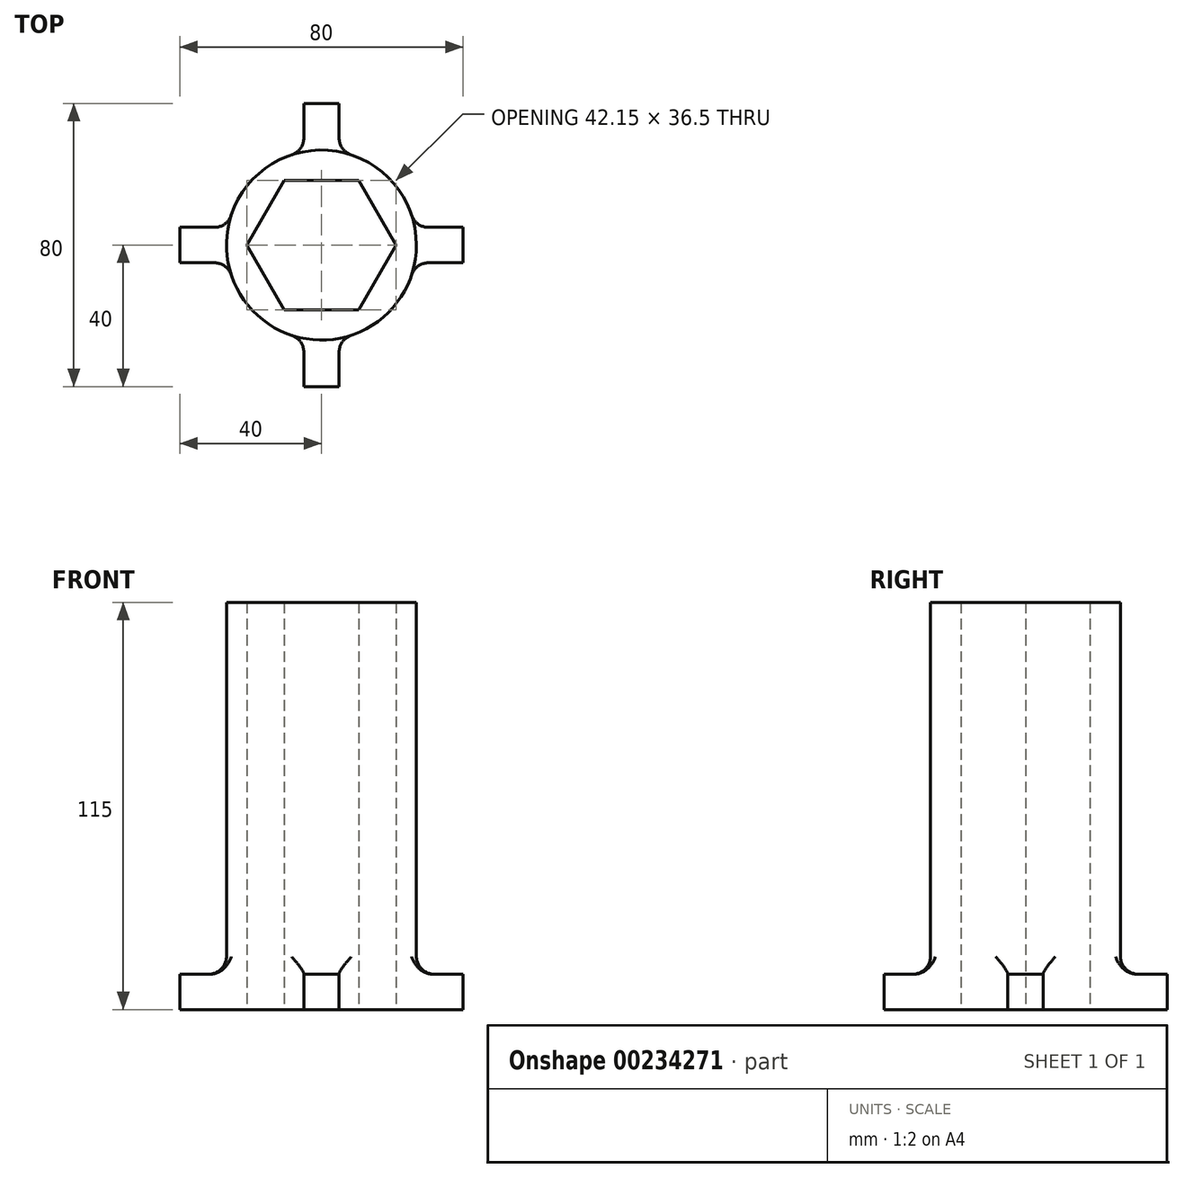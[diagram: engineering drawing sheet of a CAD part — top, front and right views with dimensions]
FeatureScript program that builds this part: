
annotation { "Feature Type Name" : "Feature", "Feature Type Description" : "" }
export const myFeature = defineFeature(function(context is Context, id is Id, definition is map)
    precondition{}
    {
        {
            var Q0;
            Q0=qCreatedBy(makeId("Top.planeOp"),FACE);
            var sketch = newSketch(context, id + "F0", { "sketchPlane" : qUnion([Q0])});
            skLineSegment(sketch, "E0", {"start": v(-10.54, 18.25) * mm, "end": v(10.54, 18.25) * mm});
            skLineSegment(sketch, "E1", {"start": v(10.54, 18.25) * mm, "end": v(21.07, 0) * mm});
            skLineSegment(sketch, "E2", {"start": v(21.07, 0) * mm, "end": v(10.54, -18.25) * mm});
            skLineSegment(sketch, "E3", {"start": v(10.54, -18.25) * mm, "end": v(-10.54, -18.25) * mm});
            skLineSegment(sketch, "E4", {"start": v(-10.54, -18.25) * mm, "end": v(-21.07, 0) * mm});
            skLineSegment(sketch, "E5", {"start": v(-21.07, 0) * mm, "end": v(-10.54, 18.25) * mm});
            skCircle(sketch, "E6", {"center": v(0, 0) * mm, "radius": 21.07 * mm, "construction": true});
            skLineSegment(sketch, "E7", {"start": v(0, 0) * mm, "end": v(-13.42, 23.25) * mm, "construction": true});
            skCircle(sketch, "E8", {"center": v(0, 0) * mm, "radius": 26.85 * mm});
            skSolve(sketch);
        }
        {
            var Q0;
            Q0=makeQuery(id+"F0.imprint","IMPRINT",FACE,{"disambiguationData":[TD([[makeQuery(id+"F0.imprint","IMPRINT",EDGE,{"derivedFrom":sQuery(id+"F0.wireOp",EDGE,"E0")}),1.0]])]});
            extrude(context, id + "F1", {"entities" : qUnion([Q0]), "depth" : 115 * mm});
        }
        {
            var Q0;
            Q0=qCreatedBy(makeId("Top.planeOp"),FACE);
            var sketch = newSketch(context, id + "F2", { "sketchPlane" : qUnion([Q0])});
            skLineSegment(sketch, "E9", {"start": v(0, 0) * mm, "end": v(-40, 0) * mm, "construction": true});
            skLineSegment(sketch, "E10", {"start": v(-40, 0) * mm, "end": v(-40, 5) * mm});
            skLineSegment(sketch, "E11", {"start": v(-40, 5) * mm, "end": v(-21.07, 5) * mm});
            skLineSegment(sketch, "E12", {"start": v(-21.07, 5) * mm, "end": v(-21.07, 0) * mm});
            skLineSegment(sketch, "E13.MirrorCS", {"start": v(-21.07, -5) * mm, "end": v(-21.07, 0) * mm});
            skLineSegment(sketch, "E14.MirrorCS", {"start": v(-40, -5) * mm, "end": v(-21.07, -5) * mm});
            skLineSegment(sketch, "E15.MirrorCS", {"start": v(-40, 0) * mm, "end": v(-40, -5) * mm});
            skLineSegment(sketch, "E16.1.0", {"start": v(-5, 40) * mm, "end": v(-5, 21.07) * mm});
            skLineSegment(sketch, "E16.1.1", {"start": v(-5, 21.07) * mm, "end": v(0, 21.07) * mm});
            skLineSegment(sketch, "E16.1.2", {"start": v(0, 40) * mm, "end": v(-5, 40) * mm});
            skLineSegment(sketch, "E16.1.3", {"start": v(5, 21.07) * mm, "end": v(0, 21.07) * mm});
            skLineSegment(sketch, "E16.1.4", {"start": v(5, 40) * mm, "end": v(5, 21.07) * mm});
            skLineSegment(sketch, "E16.1.5", {"start": v(0, 40) * mm, "end": v(5, 40) * mm});
            skLineSegment(sketch, "E16.2.0", {"start": v(40, 5) * mm, "end": v(21.07, 5) * mm});
            skLineSegment(sketch, "E16.2.1", {"start": v(21.07, 5) * mm, "end": v(21.07, 0) * mm});
            skLineSegment(sketch, "E16.2.2", {"start": v(40, 0) * mm, "end": v(40, 5) * mm});
            skLineSegment(sketch, "E16.2.3", {"start": v(21.07, -5) * mm, "end": v(21.07, 0) * mm});
            skLineSegment(sketch, "E16.2.4", {"start": v(40, -5) * mm, "end": v(21.07, -5) * mm});
            skLineSegment(sketch, "E16.2.5", {"start": v(40, 0) * mm, "end": v(40, -5) * mm});
            skLineSegment(sketch, "E16.3.0", {"start": v(5, -40) * mm, "end": v(5, -21.07) * mm});
            skLineSegment(sketch, "E16.3.1", {"start": v(5, -21.07) * mm, "end": v(0, -21.07) * mm});
            skLineSegment(sketch, "E16.3.2", {"start": v(0, -40) * mm, "end": v(5, -40) * mm});
            skLineSegment(sketch, "E16.3.3", {"start": v(-5, -21.07) * mm, "end": v(0, -21.07) * mm});
            skLineSegment(sketch, "E16.3.4", {"start": v(-5, -40) * mm, "end": v(-5, -21.07) * mm});
            skLineSegment(sketch, "E16.3.5", {"start": v(0, -40) * mm, "end": v(-5, -40) * mm});
            skPoint(sketch, "E16.center", {"position": v(0, 0) * mm});
            skLineSegment(sketch, "E16.anchor1", {"start": v(0, 0) * mm, "end": v(-40, -5) * mm, "construction": true});
            skLineSegment(sketch, "E16.anchor2", {"start": v(0, 0) * mm, "end": v(5, -40) * mm, "construction": true});
            skSolve(sketch);
        }
        {
            var Q0;
            Q0 = qSketchRegion(id + "F2", true);
            extrude(context, id + "F3", {"entities" : qUnion([Q0]), "operationType" : NewBodyOperationType.ADD, "depth" : 10 * mm});
        }
        {
            var Q0;
            Q0=makeQuery(id+"F3.boolean.opBoolean","INTERSECT",EDGE,{"derivedFrom":[makeQuery(id+"F1.opExtrude","SWEPT_FACE",FACE,{"disambiguationData":[OSD([sQuery(id+"F0.wireOp",EDGE,"E8")])]}),makeQuery(id+"F3.opExtrude","SWEPT_FACE",FACE,{"disambiguationData":[OSD([sQuery(id+"F2.wireOp",EDGE,"E16.3.0")])]})]});
            var Q1;
            Q1=makeQuery(id+"F3.boolean.opBoolean","INTERSECT",EDGE,{"derivedFrom":[makeQuery(id+"F1.opExtrude","SWEPT_FACE",FACE,{"disambiguationData":[OSD([sQuery(id+"F0.wireOp",EDGE,"E8")])]}),makeQuery(id+"F3.opExtrude","SWEPT_FACE",FACE,{"disambiguationData":[OSD([sQuery(id+"F2.wireOp",EDGE,"E16.2.4")])]})]});
            var Q2;
            Q2=makeQuery(id+"F3.boolean.opBoolean","INTERSECT",EDGE,{"derivedFrom":[makeQuery(id+"F1.opExtrude","SWEPT_FACE",FACE,{"disambiguationData":[OSD([sQuery(id+"F0.wireOp",EDGE,"E8")])]}),makeQuery(id+"F3.opExtrude","SWEPT_FACE",FACE,{"disambiguationData":[OSD([sQuery(id+"F2.wireOp",EDGE,"E16.3.4")])]})]});
            var Q3;
            Q3=makeQuery(id+"F3.boolean.opBoolean","INTERSECT",EDGE,{"derivedFrom":[makeQuery(id+"F1.opExtrude","SWEPT_FACE",FACE,{"disambiguationData":[OSD([sQuery(id+"F0.wireOp",EDGE,"E8")])]}),makeQuery(id+"F3.opExtrude","SWEPT_FACE",FACE,{"disambiguationData":[OSD([sQuery(id+"F2.wireOp",EDGE,"E14.MirrorCS")])]})]});
            var Q4;
            Q4=makeQuery(id+"F3.boolean.opBoolean","INTERSECT",EDGE,{"derivedFrom":[makeQuery(id+"F1.opExtrude","SWEPT_FACE",FACE,{"disambiguationData":[OSD([sQuery(id+"F0.wireOp",EDGE,"E8")])]}),makeQuery(id+"F3.opExtrude","SWEPT_FACE",FACE,{"disambiguationData":[OSD([sQuery(id+"F2.wireOp",EDGE,"E16.2.0")])]})]});
            var Q5;
            Q5=makeQuery(id+"F3.boolean.opBoolean","INTERSECT",EDGE,{"derivedFrom":[makeQuery(id+"F1.opExtrude","SWEPT_FACE",FACE,{"disambiguationData":[OSD([sQuery(id+"F0.wireOp",EDGE,"E8")])]}),makeQuery(id+"F3.opExtrude","SWEPT_FACE",FACE,{"disambiguationData":[OSD([sQuery(id+"F2.wireOp",EDGE,"E11")])]})]});
            var Q6;
            Q6=makeQuery(id+"F3.boolean.opBoolean","INTERSECT",EDGE,{"derivedFrom":[makeQuery(id+"F1.opExtrude","SWEPT_FACE",FACE,{"disambiguationData":[OSD([sQuery(id+"F0.wireOp",EDGE,"E8")])]}),makeQuery(id+"F3.opExtrude","SWEPT_FACE",FACE,{"disambiguationData":[OSD([sQuery(id+"F2.wireOp",EDGE,"E16.1.0")])]})]});
            var Q7;
            Q7=makeQuery(id+"F3.boolean.opBoolean","INTERSECT",EDGE,{"derivedFrom":[makeQuery(id+"F1.opExtrude","SWEPT_FACE",FACE,{"disambiguationData":[OSD([sQuery(id+"F0.wireOp",EDGE,"E8")])]}),makeQuery(id+"F3.opExtrude","SWEPT_FACE",FACE,{"disambiguationData":[OSD([sQuery(id+"F2.wireOp",EDGE,"E16.1.4")])]})]});
            fillet(context, id + "F4", {"entities" : qUnion([Q0, Q1, Q2, Q3, Q4, Q5, Q6, Q7]), "radius" : 5 * mm, "tangentPropagation" : true, "allowEdgeOverflow" : false});
        }
        {
            var Q0;
            Q0=makeQuery(id+"F3.boolean.opBoolean","INTERSECT",EDGE,{"derivedFrom":[makeQuery(id+"F1.opExtrude","SWEPT_FACE",FACE,{"disambiguationData":[OSD([sQuery(id+"F0.wireOp",EDGE,"E8")])]}),makeQuery(id+"F3.opExtrude","CAP_FACE",FACE,{"disambiguationData":[OSD([sQuery(id+"F2.wireOp",EDGE,"E16.1.0"),sQuery(id+"F2.wireOp",EDGE,"E16.1.1"),sQuery(id+"F2.wireOp",EDGE,"E16.1.2"),sQuery(id+"F2.wireOp",EDGE,"E16.1.3"),sQuery(id+"F2.wireOp",EDGE,"E16.1.4"),sQuery(id+"F2.wireOp",EDGE,"E16.1.5")])],"isStart":false})]});
            var Q1;
            Q1=makeQuery(id+"F3.boolean.opBoolean","INTERSECT",EDGE,{"derivedFrom":[makeQuery(id+"F1.opExtrude","SWEPT_FACE",FACE,{"disambiguationData":[OSD([sQuery(id+"F0.wireOp",EDGE,"E8")])]}),makeQuery(id+"F3.opExtrude","CAP_FACE",FACE,{"disambiguationData":[OSD([sQuery(id+"F2.wireOp",EDGE,"E10"),sQuery(id+"F2.wireOp",EDGE,"E11"),sQuery(id+"F2.wireOp",EDGE,"E12"),sQuery(id+"F2.wireOp",EDGE,"E13.MirrorCS"),sQuery(id+"F2.wireOp",EDGE,"E14.MirrorCS"),sQuery(id+"F2.wireOp",EDGE,"E15.MirrorCS")])],"isStart":false})]});
            var Q2;
            Q2=makeQuery(id+"F3.boolean.opBoolean","INTERSECT",EDGE,{"derivedFrom":[makeQuery(id+"F1.opExtrude","SWEPT_FACE",FACE,{"disambiguationData":[OSD([sQuery(id+"F0.wireOp",EDGE,"E8")])]}),makeQuery(id+"F3.opExtrude","CAP_FACE",FACE,{"disambiguationData":[OSD([sQuery(id+"F2.wireOp",EDGE,"E16.3.0"),sQuery(id+"F2.wireOp",EDGE,"E16.3.1"),sQuery(id+"F2.wireOp",EDGE,"E16.3.2"),sQuery(id+"F2.wireOp",EDGE,"E16.3.3"),sQuery(id+"F2.wireOp",EDGE,"E16.3.4"),sQuery(id+"F2.wireOp",EDGE,"E16.3.5")])],"isStart":false})]});
            var Q3;
            Q3=makeQuery(id+"F3.boolean.opBoolean","INTERSECT",EDGE,{"derivedFrom":[makeQuery(id+"F1.opExtrude","SWEPT_FACE",FACE,{"disambiguationData":[OSD([sQuery(id+"F0.wireOp",EDGE,"E8")])]}),makeQuery(id+"F3.opExtrude","CAP_FACE",FACE,{"disambiguationData":[OSD([sQuery(id+"F2.wireOp",EDGE,"E16.2.0"),sQuery(id+"F2.wireOp",EDGE,"E16.2.1"),sQuery(id+"F2.wireOp",EDGE,"E16.2.2"),sQuery(id+"F2.wireOp",EDGE,"E16.2.3"),sQuery(id+"F2.wireOp",EDGE,"E16.2.4"),sQuery(id+"F2.wireOp",EDGE,"E16.2.5")])],"isStart":false})]});
            fillet(context, id + "F5", {"entities" : qUnion([Q0, Q1, Q2, Q3]), "radius" : 5 * mm, "tangentPropagation" : true, "allowEdgeOverflow" : false});
        }
    });
